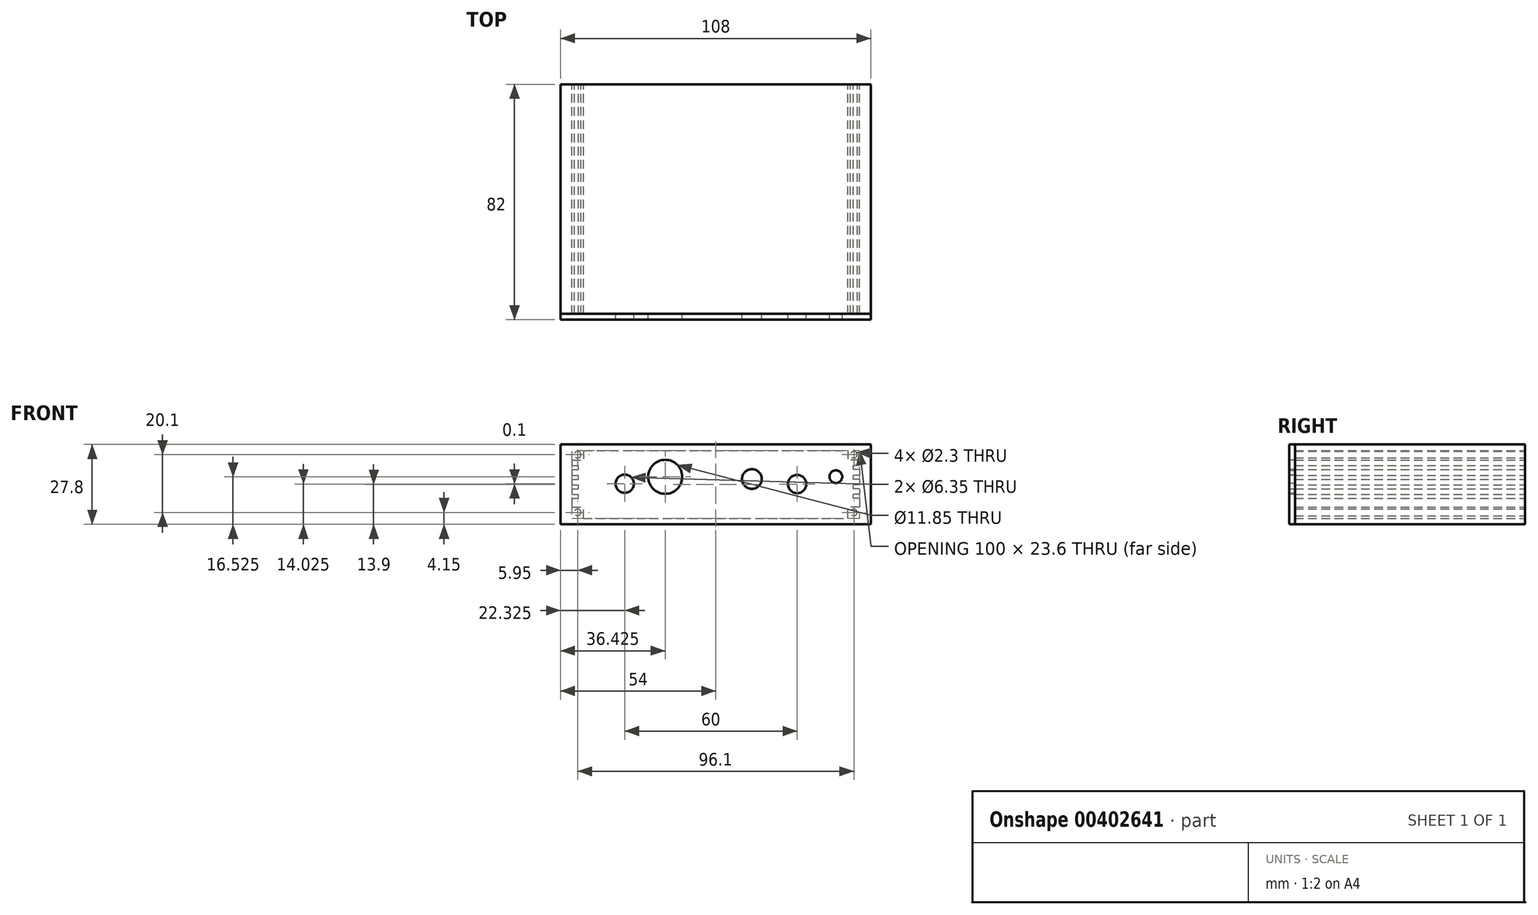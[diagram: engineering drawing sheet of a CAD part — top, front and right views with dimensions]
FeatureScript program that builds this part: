
annotation { "Feature Type Name" : "Feature", "Feature Type Description" : "" }
export const myFeature = defineFeature(function(context is Context, id is Id, definition is map)
    precondition{}
    {
        {
            var Q0;
            Q0=qCreatedBy(makeId("Front.planeOp"),FACE);
            var sketch = newSketch(context, id + "F0", { "sketchPlane" : qUnion([Q0])});
            skLineSegment(sketch, "E0.bottom", {"start": v(-50, 25.7) * mm, "end": v(50, 25.7) * mm});
            skLineSegment(sketch, "E0.top", {"start": v(-50, 0) * mm, "end": v(50, 0) * mm});
            skLineSegment(sketch, "E0.left", {"start": v(-50, 25.7) * mm, "end": v(-50, 0) * mm});
            skLineSegment(sketch, "E0.right", {"start": v(50, 25.7) * mm, "end": v(50, 0) * mm});
            skLineSegment(sketch, "E1.top", {"start": v(-50, 2.1) * mm, "end": v(50, 2.1) * mm});
            skLineSegment(sketch, "E1.left", {"start": v(-50, 0) * mm, "end": v(-50, 2.1) * mm});
            skLineSegment(sketch, "E1.right", {"start": v(50, 0) * mm, "end": v(50, 2.1) * mm});
            skLineSegment(sketch, "E2.bottom", {"start": v(-50, 0) * mm, "end": v(-46, 0) * mm});
            skLineSegment(sketch, "E2.top", {"start": v(-50, 6) * mm, "end": v(-46, 6) * mm});
            skLineSegment(sketch, "E2.left", {"start": v(-50, 0) * mm, "end": v(-50, 6) * mm});
            skLineSegment(sketch, "E2.right", {"start": v(-46, 0) * mm, "end": v(-46, 6) * mm});
            skLineSegment(sketch, "E3.bottom", {"start": v(-50, 9) * mm, "end": v(-47.8, 9) * mm});
            skLineSegment(sketch, "E3.top", {"start": v(-50, 10.4) * mm, "end": v(-47.8, 10.4) * mm});
            skLineSegment(sketch, "E3.left", {"start": v(-50, 9) * mm, "end": v(-50, 10.4) * mm});
            skLineSegment(sketch, "E3.right", {"start": v(-47.8, 9) * mm, "end": v(-47.8, 10.4) * mm});
            skLineSegment(sketch, "E4.bottom", {"start": v(-50, 12.35) * mm, "end": v(-47.8, 12.35) * mm});
            skLineSegment(sketch, "E4.top", {"start": v(-50, 13.75) * mm, "end": v(-47.8, 13.75) * mm});
            skLineSegment(sketch, "E4.left", {"start": v(-50, 12.35) * mm, "end": v(-50, 13.75) * mm});
            skLineSegment(sketch, "E4.right", {"start": v(-47.8, 12.35) * mm, "end": v(-47.8, 13.75) * mm});
            skLineSegment(sketch, "E5.bottom", {"start": v(-50, 15.7) * mm, "end": v(-47.8, 15.7) * mm});
            skLineSegment(sketch, "E5.top", {"start": v(-50, 17.1) * mm, "end": v(-47.8, 17.1) * mm});
            skLineSegment(sketch, "E5.left", {"start": v(-50, 15.7) * mm, "end": v(-50, 17.1) * mm});
            skLineSegment(sketch, "E5.right", {"start": v(-47.8, 15.7) * mm, "end": v(-47.8, 17.1) * mm});
            skLineSegment(sketch, "E6.bottom", {"start": v(-50, 19.05) * mm, "end": v(-47.8, 19.05) * mm});
            skLineSegment(sketch, "E6.top", {"start": v(-50, 20.45) * mm, "end": v(-47.8, 20.45) * mm});
            skLineSegment(sketch, "E6.left", {"start": v(-50, 19.05) * mm, "end": v(-50, 20.45) * mm});
            skLineSegment(sketch, "E6.right", {"start": v(-47.8, 19.05) * mm, "end": v(-47.8, 20.45) * mm});
            skLineSegment(sketch, "E7.bottom", {"start": v(-50, 25.7) * mm, "end": v(-46, 25.7) * mm});
            skLineSegment(sketch, "E7.top", {"start": v(-50, 22.4) * mm, "end": v(-46, 22.4) * mm});
            skLineSegment(sketch, "E7.left", {"start": v(-50, 25.7) * mm, "end": v(-50, 22.4) * mm});
            skLineSegment(sketch, "E7.right", {"start": v(-46, 25.7) * mm, "end": v(-46, 22.4) * mm});
            skLineSegment(sketch, "E8.bottom", {"start": v(-50, 25.7) * mm, "end": v(-54, 25.7) * mm});
            skLineSegment(sketch, "E8.top", {"start": v(-50, 0) * mm, "end": v(-54, 0) * mm});
            skLineSegment(sketch, "E8.right", {"start": v(-54, 25.7) * mm, "end": v(-54, 0) * mm});
            skLineSegment(sketch, "E9.bottom", {"start": v(50, 25.7) * mm, "end": v(-54, 25.7) * mm});
            skLineSegment(sketch, "E9.top", {"start": v(50, 27.8) * mm, "end": v(-54, 27.8) * mm});
            skLineSegment(sketch, "E9.left", {"start": v(50, 25.7) * mm, "end": v(50, 27.8) * mm});
            skLineSegment(sketch, "E9.right", {"start": v(-54, 25.7) * mm, "end": v(-54, 27.8) * mm});
            skLineSegment(sketch, "E10.MirrorCS", {"start": v(50, 25.7) * mm, "end": v(50, 22.4) * mm});
            skLineSegment(sketch, "E11.MirrorCS", {"start": v(50, 12.35) * mm, "end": v(50, 13.75) * mm});
            skLineSegment(sketch, "E12.MirrorCS", {"start": v(50, 15.7) * mm, "end": v(50, 17.1) * mm});
            skLineSegment(sketch, "E13.MirrorCS", {"start": v(50, 13.75) * mm, "end": v(47.8, 13.75) * mm});
            skLineSegment(sketch, "E14.MirrorCS", {"start": v(50, 17.1) * mm, "end": v(47.8, 17.1) * mm});
            skLineSegment(sketch, "E15.MirrorCS", {"start": v(50, 9) * mm, "end": v(50, 10.4) * mm});
            skLineSegment(sketch, "E16.MirrorCS", {"start": v(50, 12.35) * mm, "end": v(47.8, 12.35) * mm});
            skLineSegment(sketch, "E17.MirrorCS", {"start": v(47.8, 12.35) * mm, "end": v(47.8, 13.75) * mm});
            skLineSegment(sketch, "E18.MirrorCS", {"start": v(50, 10.4) * mm, "end": v(47.8, 10.4) * mm});
            skLineSegment(sketch, "E19.MirrorCS", {"start": v(50, 15.7) * mm, "end": v(47.8, 15.7) * mm});
            skLineSegment(sketch, "E20.MirrorCS", {"start": v(50, 9) * mm, "end": v(47.8, 9) * mm});
            skLineSegment(sketch, "E21.MirrorCS", {"start": v(50, 20.45) * mm, "end": v(47.8, 20.45) * mm});
            skLineSegment(sketch, "E22.MirrorCS", {"start": v(50, 19.05) * mm, "end": v(47.8, 19.05) * mm});
            skLineSegment(sketch, "E23.MirrorCS", {"start": v(50, 19.05) * mm, "end": v(50, 20.45) * mm});
            skLineSegment(sketch, "E24.MirrorCS", {"start": v(47.8, 15.7) * mm, "end": v(47.8, 17.1) * mm});
            skLineSegment(sketch, "E25.MirrorCS", {"start": v(47.8, 19.05) * mm, "end": v(47.8, 20.45) * mm});
            skLineSegment(sketch, "E26.MirrorCS", {"start": v(54, 25.7) * mm, "end": v(54, 27.8) * mm});
            skLineSegment(sketch, "E27.MirrorCS", {"start": v(50, 25.7) * mm, "end": v(54, 25.7) * mm});
            skLineSegment(sketch, "E28.MirrorCS", {"start": v(47.8, 9) * mm, "end": v(47.8, 10.4) * mm});
            skLineSegment(sketch, "E29.MirrorCS", {"start": v(50, 0) * mm, "end": v(50, 6) * mm});
            skLineSegment(sketch, "E30.MirrorCS", {"start": v(46, 25.7) * mm, "end": v(46, 22.4) * mm});
            skLineSegment(sketch, "E31.MirrorCS", {"start": v(50, 0) * mm, "end": v(54, 0) * mm});
            skLineSegment(sketch, "E32.MirrorCS", {"start": v(50, 25.7) * mm, "end": v(46, 25.7) * mm});
            skLineSegment(sketch, "E33.MirrorCS", {"start": v(50, 0) * mm, "end": v(46, 0) * mm});
            skLineSegment(sketch, "E34.MirrorCS", {"start": v(50, 6) * mm, "end": v(46, 6) * mm});
            skLineSegment(sketch, "E35.MirrorCS", {"start": v(50, 22.4) * mm, "end": v(46, 22.4) * mm});
            skLineSegment(sketch, "E36.MirrorCS", {"start": v(54, 25.7) * mm, "end": v(54, 0) * mm});
            skLineSegment(sketch, "E37.MirrorCS", {"start": v(46, 0) * mm, "end": v(46, 6) * mm});
            skLineSegment(sketch, "E38", {"start": v(50, 27.8) * mm, "end": v(54, 27.8) * mm});
            skCircle(sketch, "E39", {"center": v(-48.05, 24.25) * mm, "radius": 1.15 * mm});
            skCircle(sketch, "E40", {"center": v(-48.05, 4.15) * mm, "radius": 1.15 * mm});
            skCircle(sketch, "E41.MirrorC", {"center": v(48.05, 24.25) * mm, "radius": 1.15 * mm});
            skCircle(sketch, "E42.MirrorC", {"center": v(48.05, 4.15) * mm, "radius": 1.15 * mm});
            skSolve(sketch);
        }
        {
            var Q0;
            Q0=makeQuery(id+"F0.imprint","IMPRINT",FACE,{"disambiguationData":[TD([[makeQuery(id+"F0.imprint","IMPRINT",EDGE,{"derivedFrom":sQuery(id+"F0.wireOp",EDGE,"E9.top")}),1.0]])]});
            var Q1;
            {var subQ8=sQuery(id+"F0.wireOp",EDGE,"E8.top");Q1=makeQuery(id+"F0.imprint","IMPRINT",FACE,{"disambiguationData":[TD([[makeQuery(id+"F0.imprint","IMPRINT",EDGE,{"derivedFrom":subQ8}),-1.0]])]});}
            var Q2;
            {var subQ4=sQuery(id+"F0.wireOp",EDGE,"E7.top");Q2=makeQuery(id+"F0.imprint","IMPRINT",FACE,{"disambiguationData":[TD([[makeQuery(id+"F0.imprint","IMPRINT",EDGE,{"derivedFrom":subQ4}),1.0]])]});}
            var Q3;
            {var subQ3=sQuery(id+"F0.wireOp",EDGE,"E2.top");Q3=makeQuery(id+"F0.imprint","IMPRINT",FACE,{"disambiguationData":[TD([[makeQuery(id+"F0.imprint","IMPRINT",EDGE,{"derivedFrom":subQ3}),-1.0]])]});}
            var Q4;
            {var subQ5=sQuery(id+"F0.wireOp",EDGE,"E2.bottom");Q4=makeQuery(id+"F0.imprint","IMPRINT",FACE,{"disambiguationData":[TD([[makeQuery(id+"F0.imprint","IMPRINT",EDGE,{"derivedFrom":subQ5}),1.0]])]});}
            var Q5;
            {var subQ0=sQuery(id+"F0.wireOp",EDGE,"E0.top");Q5=makeQuery(id+"F0.imprint","IMPRINT",FACE,{"disambiguationData":[TD([[makeQuery(id+"F0.imprint","IMPRINT",EDGE,{"derivedFrom":subQ0}),1.0]])]});}
            var Q6;
            {var subQ5=sQuery(id+"F0.wireOp",EDGE,"E33.MirrorCS");Q6=makeQuery(id+"F0.imprint","IMPRINT",FACE,{"disambiguationData":[TD([[makeQuery(id+"F0.imprint","IMPRINT",EDGE,{"derivedFrom":subQ5}),-1.0]])]});}
            var Q7;
            {var subQ8=sQuery(id+"F0.wireOp",EDGE,"E27.MirrorCS");Q7=makeQuery(id+"F0.imprint","IMPRINT",FACE,{"disambiguationData":[TD([[makeQuery(id+"F0.imprint","IMPRINT",EDGE,{"derivedFrom":subQ8}),-1.0]])]});}
            var Q8;
            {var subQ0=sQuery(id+"F0.wireOp",EDGE,"E34.MirrorCS");Q8=makeQuery(id+"F0.imprint","IMPRINT",FACE,{"disambiguationData":[TD([[makeQuery(id+"F0.imprint","IMPRINT",EDGE,{"derivedFrom":subQ0}),1.0]])]});}
            var Q9;
            {var subQ0=sQuery(id+"F0.wireOp",EDGE,"E18.MirrorCS");Q9=makeQuery(id+"F0.imprint","IMPRINT",FACE,{"disambiguationData":[TD([[makeQuery(id+"F0.imprint","IMPRINT",EDGE,{"derivedFrom":subQ0}),1.0]])]});}
            var Q10;
            {var subQ0=sQuery(id+"F0.wireOp",EDGE,"E13.MirrorCS");Q10=makeQuery(id+"F0.imprint","IMPRINT",FACE,{"disambiguationData":[TD([[makeQuery(id+"F0.imprint","IMPRINT",EDGE,{"derivedFrom":subQ0}),1.0]])]});}
            var Q11;
            {var subQ0=sQuery(id+"F0.wireOp",EDGE,"E14.MirrorCS");Q11=makeQuery(id+"F0.imprint","IMPRINT",FACE,{"disambiguationData":[TD([[makeQuery(id+"F0.imprint","IMPRINT",EDGE,{"derivedFrom":subQ0}),1.0]])]});}
            var Q12;
            {var subQ0=sQuery(id+"F0.wireOp",EDGE,"E21.MirrorCS");Q12=makeQuery(id+"F0.imprint","IMPRINT",FACE,{"disambiguationData":[TD([[makeQuery(id+"F0.imprint","IMPRINT",EDGE,{"derivedFrom":subQ0}),1.0]])]});}
            var Q13;
            Q13=makeQuery(id+"F0.imprint","IMPRINT",FACE,{"disambiguationData":[TD([[makeQuery(id+"F0.imprint","IMPRINT",EDGE,{"derivedFrom":sQuery(id+"F0.wireOp",EDGE,"E30.MirrorCS")}),1.0]])]});
            var Q14;
            Q14=makeQuery(id+"F0.imprint","IMPRINT",FACE,{"disambiguationData":[TD([[makeQuery(id+"F0.imprint","IMPRINT",EDGE,{"derivedFrom":sQuery(id+"F0.wireOp",EDGE,"E9.left")}),-1.0]])]});
            var Q15;
            {var subQ0=sQuery(id+"F0.wireOp",EDGE,"E3.bottom");Q15=makeQuery(id+"F0.imprint","IMPRINT",FACE,{"disambiguationData":[TD([[makeQuery(id+"F0.imprint","IMPRINT",EDGE,{"derivedFrom":subQ0}),1.0]])]});}
            var Q16;
            {var subQ0=sQuery(id+"F0.wireOp",EDGE,"E4.bottom");Q16=makeQuery(id+"F0.imprint","IMPRINT",FACE,{"disambiguationData":[TD([[makeQuery(id+"F0.imprint","IMPRINT",EDGE,{"derivedFrom":subQ0}),1.0]])]});}
            var Q17;
            {var subQ0=sQuery(id+"F0.wireOp",EDGE,"E5.bottom");Q17=makeQuery(id+"F0.imprint","IMPRINT",FACE,{"disambiguationData":[TD([[makeQuery(id+"F0.imprint","IMPRINT",EDGE,{"derivedFrom":subQ0}),1.0]])]});}
            var Q18;
            {var subQ0=sQuery(id+"F0.wireOp",EDGE,"E6.bottom");Q18=makeQuery(id+"F0.imprint","IMPRINT",FACE,{"disambiguationData":[TD([[makeQuery(id+"F0.imprint","IMPRINT",EDGE,{"derivedFrom":subQ0}),1.0]])]});}
            extrude(context, id + "F1", {"entities" : qUnion([Q0, Q1, Q2, Q3, Q4, Q5, Q6, Q7, Q8, Q9, Q10, Q11, Q12, Q13, Q14, Q15, Q16, Q17, Q18]), "depth" : 80 * mm});
        }
        {
            var Q0;
            Q0=qCreatedBy(makeId("Front.planeOp"),FACE);
            var sketch = newSketch(context, id + "F2", { "sketchPlane" : qUnion([Q0])});
            skLineSegment(sketch, "E43.bottom", {"start": v(-54, 27.8) * mm, "end": v(54, 27.8) * mm});
            skLineSegment(sketch, "E43.top", {"start": v(-54, 0) * mm, "end": v(54, 0) * mm});
            skLineSegment(sketch, "E43.left", {"start": v(-54, 27.8) * mm, "end": v(-54, 0) * mm});
            skLineSegment(sketch, "E43.right", {"start": v(54, 27.8) * mm, "end": v(54, 0) * mm});
            skCircle(sketch, "E44", {"center": v(-31.67, 14.12) * mm, "radius": 3.17 * mm});
            skLineSegment(sketch, "E45", {"start": v(-54, 0.35) * mm, "end": v(54, 0.35) * mm});
            skCircle(sketch, "E46", {"center": v(-17.57, 16.53) * mm, "radius": 5.92 * mm});
            skCircle(sketch, "E47", {"center": v(12.58, 15.78) * mm, "radius": 3.43 * mm});
            skCircle(sketch, "E48", {"center": v(28.32, 14.02) * mm, "radius": 3.17 * mm});
            skCircle(sketch, "E49", {"center": v(41.77, 16.57) * mm, "radius": 2.23 * mm});
            skLineSegment(sketch, "E50.left", {"start": v(-54, 0.35) * mm, "end": v(-54, 0) * mm});
            skLineSegment(sketch, "E50.right", {"start": v(54, 0.35) * mm, "end": v(54, 0) * mm});
            skSolve(sketch);
        }
        {
            var Q0;
            Q0 = qSketchRegion(id + "F2", true);
            extrude(context, id + "F3", {"entities" : qUnion([Q0]), "depth" : (80 + 2) * mm, "hasSecondDirection" : true, "secondDirectionOppositeDirection" : false, "secondDirectionDepth" : 80 * mm});
        }
    });
